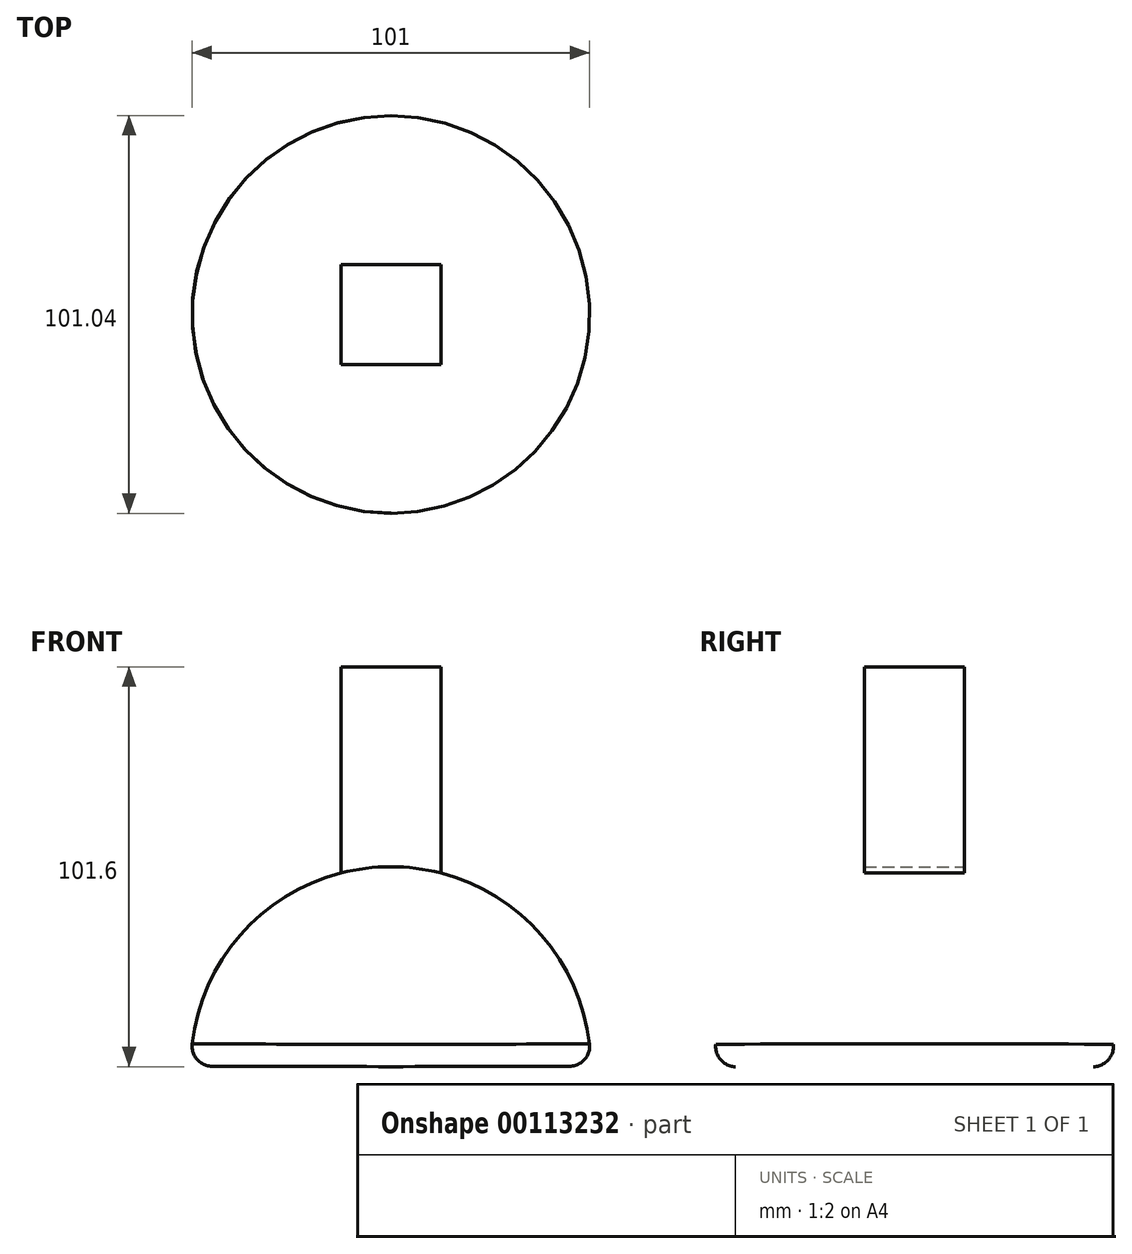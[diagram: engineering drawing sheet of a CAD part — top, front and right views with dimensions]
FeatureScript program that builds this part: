
annotation { "Feature Type Name" : "Feature", "Feature Type Description" : "" }
export const myFeature = defineFeature(function(context is Context, id is Id, definition is map)
    precondition{}
    {
        {
            var Q0;
            Q0=qCreatedBy(makeId("Front.planeOp"),FACE);
            var sketch = newSketch(context, id + "F0", { "sketchPlane" : qUnion([Q0])});
            skLineSegment(sketch, "E0", {"start": v(0, 0) * mm, "end": v(0, 50.8) * mm});
            skLineSegment(sketch, "E1", {"start": v(0, 0) * mm, "end": v(0, -50.8) * mm});
            skArc(sketch, "E2", {"start": v(50.8, -50.8) * mm, "mid": v(0, 0) * mm, "end": v(-50.8, -50.8) * mm});
            skLineSegment(sketch, "E3", {"start": v(50.8, -50.8) * mm, "end": v(-50.8, -50.8) * mm});
            skLineSegment(sketch, "E4", {"start": v(-12.7, 50.8) * mm, "end": v(-12.7, -1.61) * mm});
            skLineSegment(sketch, "E5", {"start": v(12.7, 50.8) * mm, "end": v(12.7, -1.61) * mm});
            skLineSegment(sketch, "E6", {"start": v(-12.7, 50.8) * mm, "end": v(12.7, 50.8) * mm});
            skSolve(sketch);
        }
        {
            var Q0;
            Q0=qCreatedBy(makeId("Right.planeOp"),FACE);
            var sketch = newSketch(context, id + "F1", { "sketchPlane" : qUnion([Q0])});
            skLineSegment(sketch, "E7", {"start": v(0, 0) * mm, "end": v(0, -50.8) * mm});
            skArc(sketch, "E8", {"start": v(50.8, -50.8) * mm, "mid": v(0, 0) * mm, "end": v(-50.8, -50.8) * mm});
            skLineSegment(sketch, "E9", {"start": v(-50.8, -50.8) * mm, "end": v(50.8, -50.8) * mm});
            skLineSegment(sketch, "E10", {"start": v(0, 0) * mm, "end": v(0, 50.8) * mm});
            skLineSegment(sketch, "E11", {"start": v(0, 50.8) * mm, "end": v(-12.7, 50.8) * mm});
            skLineSegment(sketch, "E12", {"start": v(-12.7, 50.8) * mm, "end": v(-12.7, -1.61) * mm});
            skLineSegment(sketch, "E13", {"start": v(0, 50.8) * mm, "end": v(12.7, 50.8) * mm});
            skLineSegment(sketch, "E14", {"start": v(12.7, 50.8) * mm, "end": v(12.7, -1.61) * mm});
            skSolve(sketch);
        }
        {
            var Q0;
            {var subQ0=sQuery(id+"F1.wireOp",EDGE,"E7");Q0=makeQuery(id+"F1.imprint","IMPRINT",FACE,{"disambiguationData":[TD([[makeQuery(id+"F1.imprint","IMPRINT",EDGE,{"derivedFrom":subQ0}),1.0]])]});}
            var Q1;
            {var subQ0=sQuery(id+"F1.wireOp",EDGE,"E7");Q1=makeQuery(id+"F1.imprint","IMPRINT",FACE,{"disambiguationData":[TD([[makeQuery(id+"F1.imprint","IMPRINT",EDGE,{"derivedFrom":subQ0}),-1.0]])]});}
            var Q2;
            Q2=sQuery(id+"F1.wireOp",EDGE,"E9");
            revolve(context, id + "F2", {"entities" : qUnion([Q0, Q1]), "axis" : qUnion([Q2]), "revolveType" : RevolveType.TWO_DIRECTIONS, "angle" : 89.85 * degree, "angleBack" : 270.16 * degree});
        }
        {
            var Q0;
            {var subQ0=sQuery(id+"F0.wireOp",EDGE,"E0");Q0=makeQuery(id+"F0.imprint","IMPRINT",FACE,{"disambiguationData":[TD([[makeQuery(id+"F0.imprint","IMPRINT",EDGE,{"derivedFrom":subQ0}),-1.0]])]});}
            var Q1;
            {var subQ0=sQuery(id+"F0.wireOp",EDGE,"E0");Q1=makeQuery(id+"F0.imprint","IMPRINT",FACE,{"disambiguationData":[TD([[makeQuery(id+"F0.imprint","IMPRINT",EDGE,{"derivedFrom":subQ0}),1.0]])]});}
            extrude(context, id + "F3", {"entities" : qUnion([Q0, Q1]), "endBound" : BoundingType.SYMMETRIC, "depth" : 25.4 * mm});
        }
        {
            var Q0;
            Q0=makeQuery(id+"F2.opRevolve","SWEPT_FACE",FACE,{"disambiguationData":[OSD([sQuery(id+"F1.wireOp",EDGE,"E8")])]});
            fillet(context, id + "F4", {"entities" : qUnion([Q0]), "radius" : 5.08 * mm, "tangentPropagation" : true, "allowEdgeOverflow" : false});
        }
    });
